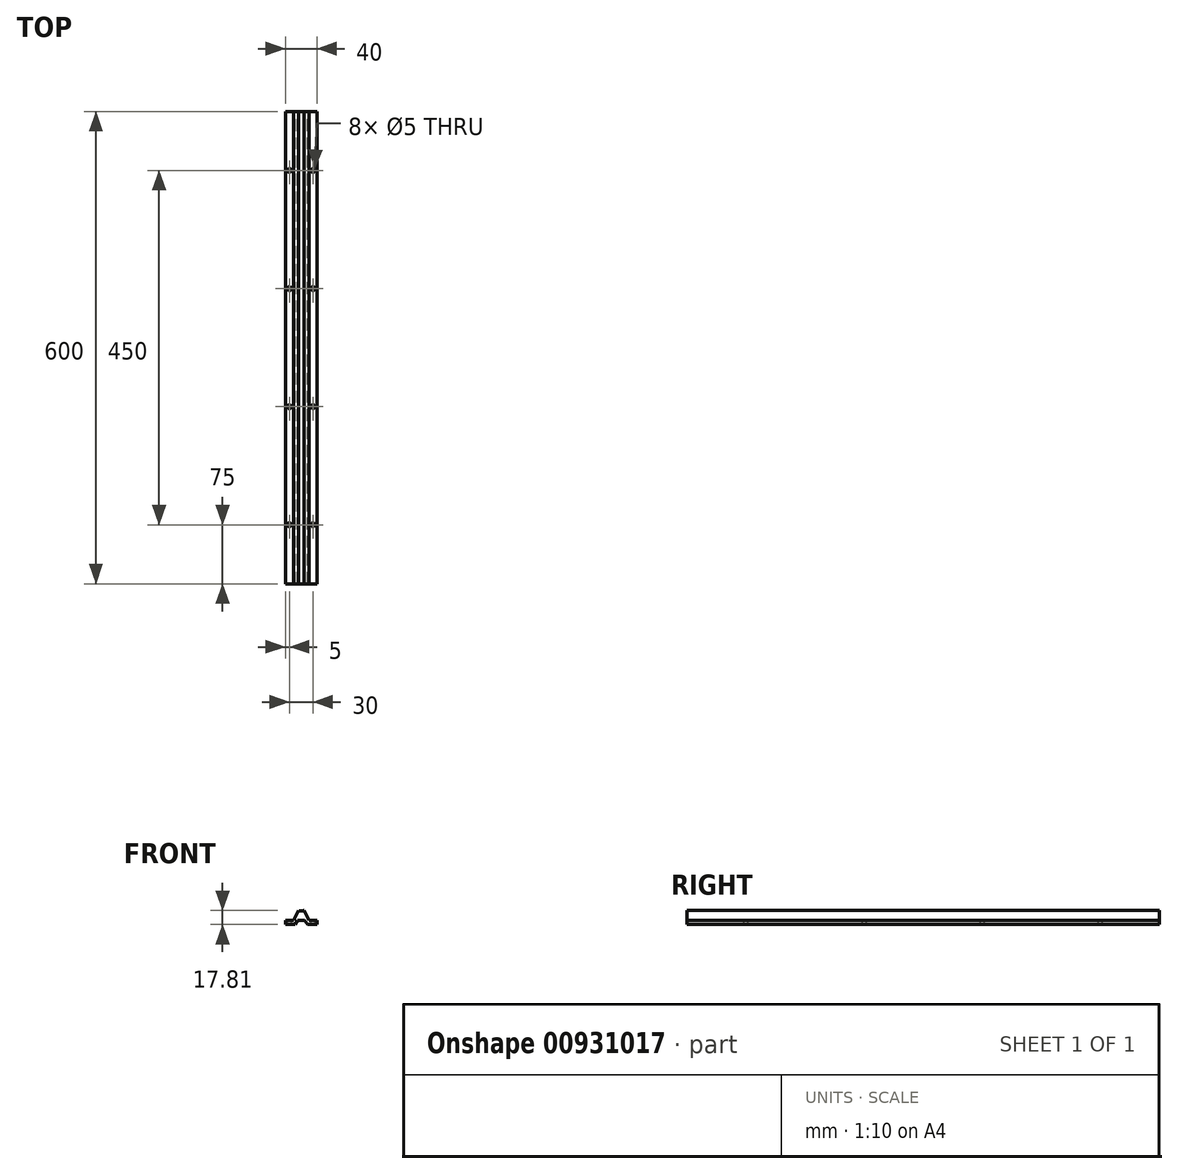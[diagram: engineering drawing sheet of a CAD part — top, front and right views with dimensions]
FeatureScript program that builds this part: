
annotation { "Feature Type Name" : "Feature", "Feature Type Description" : "" }
export const myFeature = defineFeature(function(context is Context, id is Id, definition is map)
    precondition{}
    {
        {
            var Q0;
            Q0=qCreatedBy(makeId("Front.planeOp"),FACE);
            var sketch = newSketch(context, id + "F0", { "sketchPlane" : qUnion([Q0])});
            skCircle(sketch, "E0", {"center": v(0, 0) * mm, "radius": 8 * mm, "construction": true});
            skLineSegment(sketch, "E1", {"start": v(0, 8) * mm, "end": v(0, -8) * mm, "construction": true});
            skLineSegment(sketch, "E2", {"start": v(0, -7.2) * mm, "end": v(3.5, -7.2) * mm, "construction": true});
            skLineSegment(sketch, "E3", {"start": v(0, -8) * mm, "end": v(0, -20) * mm, "construction": true});
            skLineSegment(sketch, "E4", {"start": v(0, -20) * mm, "end": v(4.5, -20) * mm});
            skLineSegment(sketch, "E5", {"start": v(0, -20) * mm, "end": v(0, -25) * mm, "construction": true});
            skLineSegment(sketch, "E6", {"start": v(0, -25) * mm, "end": v(8, -25) * mm, "construction": true});
            skLineSegment(sketch, "E7", {"start": v(4.5, -20) * mm, "end": v(8, -25) * mm});
            skLineSegment(sketch, "E8", {"start": v(8, -25) * mm, "end": v(20, -25) * mm});
            skLineSegment(sketch, "E9", {"start": v(20, -25) * mm, "end": v(20, -20) * mm});
            skLineSegment(sketch, "E10", {"start": v(20, -20) * mm, "end": v(10, -20) * mm});
            skLineSegment(sketch, "E11", {"start": v(10, -20) * mm, "end": v(3.5, -7.2) * mm});
            skArc(sketch, "E12", {"start": v(0, -8) * mm, "mid": v(1.8, -7.8) * mm, "end": v(3.5, -7.2) * mm});
            skLineSegment(sketch, "E13.MirrorCS", {"start": v(-10, -20) * mm, "end": v(-3.5, -7.2) * mm});
            skLineSegment(sketch, "E14.MirrorCS", {"start": v(-20, -20) * mm, "end": v(-10, -20) * mm});
            skLineSegment(sketch, "E15.MirrorCS", {"start": v(-20, -25) * mm, "end": v(-20, -20) * mm});
            skLineSegment(sketch, "E16.MirrorCS", {"start": v(-8, -25) * mm, "end": v(-20, -25) * mm});
            skLineSegment(sketch, "E17.MirrorCS", {"start": v(-4.5, -20) * mm, "end": v(-8, -25) * mm});
            skLineSegment(sketch, "E18.MirrorCS", {"start": v(0, -20) * mm, "end": v(-4.5, -20) * mm});
            skArc(sketch, "E19.MirrorCS", {"start": v(0, -8) * mm, "mid": v(-1.8, -7.8) * mm, "end": v(-3.5, -7.2) * mm});
            skSolve(sketch);
        }
        {
            var Q0;
            Q0=qSketchRegion(id+"F0",true);
            extrude(context, id + "F1", {"entities" : qUnion([Q0]), "depth" : 600 * mm, "offsetDistance" : 25 * mm});
        }
        {
            var Q0;
            Q0=makeQuery(id+"F1.opExtrude","SWEPT_FACE",FACE,{"disambiguationData":[OSD([sQuery(id+"F0.wireOp",EDGE,"E10")])]});
            var sketch = newSketch(context, id + "F2", { "sketchPlane" : qUnion([Q0])});
            skCircle(sketch, "E20", {"center": v(15, -525) * mm, "radius": 2.5 * mm});
            skCircle(sketch, "E21", {"center": v(15, -375) * mm, "radius": 2.5 * mm});
            skCircle(sketch, "E22.MirrorC", {"center": v(-15, -375) * mm, "radius": 2.5 * mm});
            skCircle(sketch, "E23.MirrorC", {"center": v(-15, -525) * mm, "radius": 2.5 * mm});
            skCircle(sketch, "E24.0.1.0", {"center": v(-15, -225) * mm, "radius": 2.5 * mm});
            skCircle(sketch, "E24.0.1.1", {"center": v(15, -225) * mm, "radius": 2.5 * mm});
            skCircle(sketch, "E24.0.2.0", {"center": v(-15, -75) * mm, "radius": 2.5 * mm});
            skCircle(sketch, "E24.0.2.1", {"center": v(15, -75) * mm, "radius": 2.5 * mm});
            skLineSegment(sketch, "E24.direction1", {"start": v(-15, -375) * mm, "end": v(0.9, -375) * mm, "construction": true});
            skLineSegment(sketch, "E24.direction2", {"start": v(-15, -375) * mm, "end": v(-15, -225) * mm, "construction": true});
            skSolve(sketch);
        }
        {
            var Q0;
            Q0=qSketchRegion(id+"F2",true);
            var Q1;
            Q1=makeQuery(id+"F1.opExtrude","SWEPT_FACE",FACE,{"disambiguationData":[OSD([sQuery(id+"F0.wireOp",EDGE,"E8")])]});
            extrude(context, id + "F3", {"entities" : qUnion([Q0]), "operationType" : NewBodyOperationType.REMOVE, "endBound" : BoundingType.UP_TO_SURFACE, "oppositeDirection" : true, "depth" : 5 * mm, "endBoundEntityFace" : qUnion([Q1]), "offsetDistance" : 25 * mm});
        }
    });
